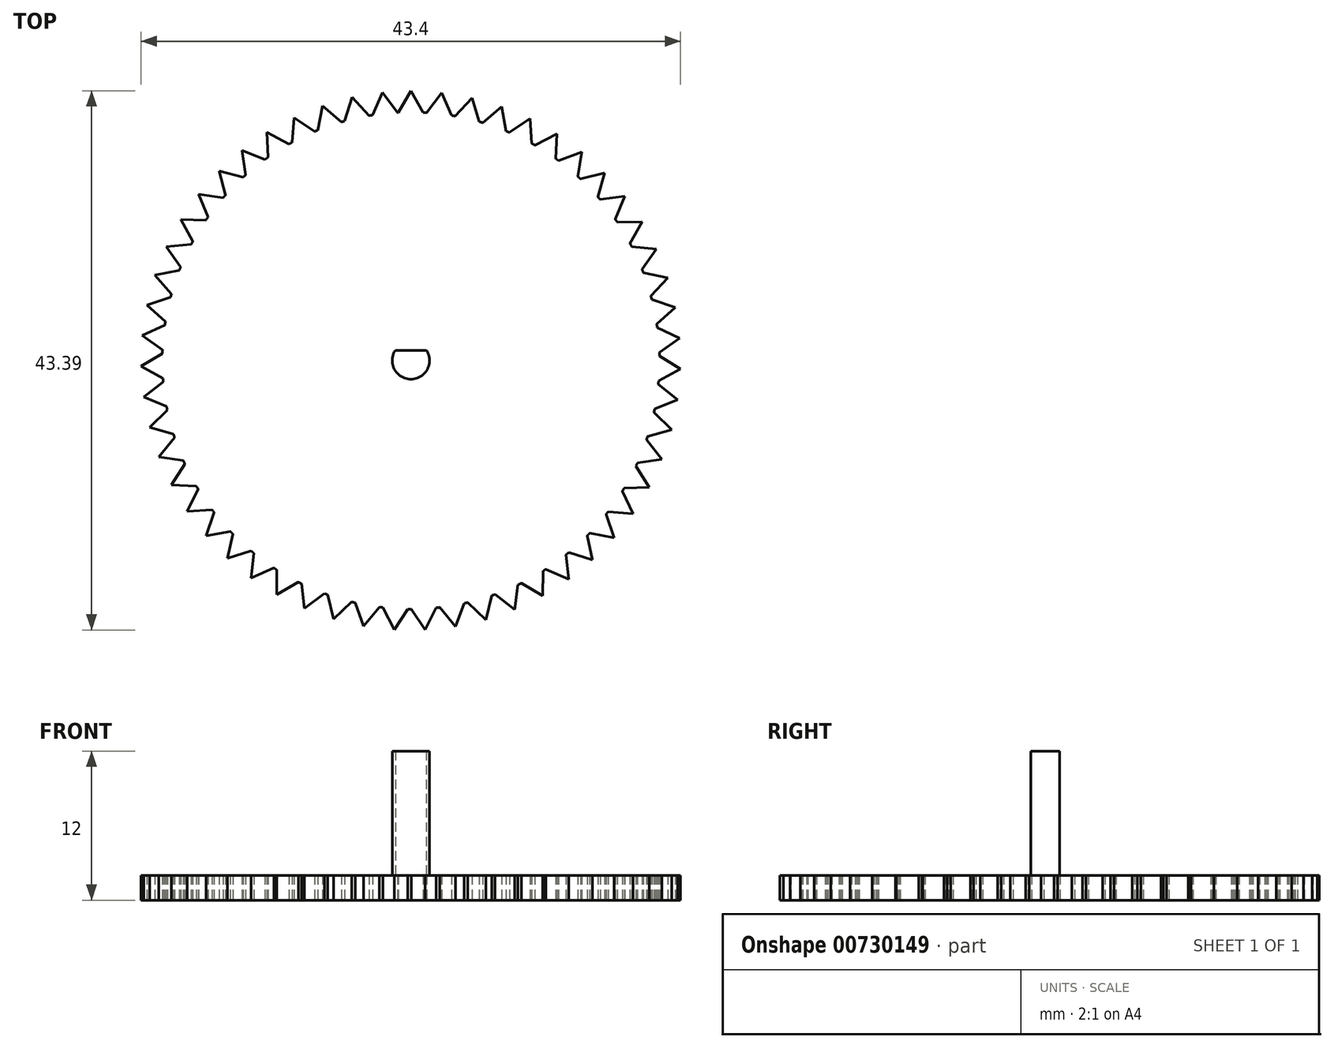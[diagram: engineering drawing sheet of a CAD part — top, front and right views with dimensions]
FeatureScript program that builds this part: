
annotation { "Feature Type Name" : "Feature", "Feature Type Description" : "" }
export const myFeature = defineFeature(function(context is Context, id is Id, definition is map)
    precondition{}
    {
        {
            var Q0;
            Q0=qCreatedBy(makeId("Top.planeOp"),FACE);
            var sketch = newSketch(context, id + "F0", { "sketchPlane" : qUnion([Q0])});
            skCircle(sketch, "E0", {"center": v(0, 0) * mm, "radius": 20 * mm});
            skLineSegment(sketch, "E1", {"start": v(-1, 19.97) * mm, "end": v(0, 21.7) * mm});
            skLineSegment(sketch, "E2", {"start": v(0, 21.7) * mm, "end": v(1, 19.97) * mm});
            skLineSegment(sketch, "E3.1.0", {"start": v(1.29, 19.96) * mm, "end": v(2.48, 21.57) * mm});
            skLineSegment(sketch, "E3.1.1", {"start": v(2.48, 21.57) * mm, "end": v(3.27, 19.73) * mm});
            skLineSegment(sketch, "E3.2.0", {"start": v(3.56, 19.68) * mm, "end": v(4.92, 21.14) * mm});
            skLineSegment(sketch, "E3.2.1", {"start": v(4.92, 21.14) * mm, "end": v(5.5, 19.23) * mm});
            skLineSegment(sketch, "E3.3.0", {"start": v(5.78, 19.15) * mm, "end": v(7.3, 20.44) * mm});
            skLineSegment(sketch, "E3.3.1", {"start": v(7.3, 20.44) * mm, "end": v(7.66, 18.47) * mm});
            skLineSegment(sketch, "E3.4.0", {"start": v(7.93, 18.36) * mm, "end": v(9.6, 19.47) * mm});
            skLineSegment(sketch, "E3.4.1", {"start": v(9.6, 19.47) * mm, "end": v(9.72, 17.48) * mm});
            skLineSegment(sketch, "E3.5.0", {"start": v(9.97, 17.34) * mm, "end": v(11.75, 18.25) * mm});
            skLineSegment(sketch, "E3.5.1", {"start": v(11.75, 18.25) * mm, "end": v(11.65, 16.25) * mm});
            skLineSegment(sketch, "E3.6.0", {"start": v(11.89, 16.08) * mm, "end": v(13.76, 16.79) * mm});
            skLineSegment(sketch, "E3.6.1", {"start": v(13.76, 16.79) * mm, "end": v(13.43, 14.82) * mm});
            skLineSegment(sketch, "E3.7.0", {"start": v(13.65, 14.62) * mm, "end": v(15.59, 15.1) * mm});
            skLineSegment(sketch, "E3.7.1", {"start": v(15.59, 15.1) * mm, "end": v(15.04, 13.19) * mm});
            skLineSegment(sketch, "E3.8.0", {"start": v(15.23, 12.97) * mm, "end": v(17.2, 13.23) * mm});
            skLineSegment(sketch, "E3.8.1", {"start": v(17.2, 13.23) * mm, "end": v(16.44, 11.38) * mm});
            skLineSegment(sketch, "E3.9.0", {"start": v(16.6, 11.15) * mm, "end": v(18.6, 11.18) * mm});
            skLineSegment(sketch, "E3.9.1", {"start": v(18.6, 11.18) * mm, "end": v(17.64, 9.43) * mm});
            skLineSegment(sketch, "E3.10.0", {"start": v(17.77, 9.18) * mm, "end": v(19.76, 8.98) * mm});
            skLineSegment(sketch, "E3.10.1", {"start": v(19.76, 8.98) * mm, "end": v(18.6, 7.36) * mm});
            skLineSegment(sketch, "E3.11.0", {"start": v(18.7, 7.09) * mm, "end": v(20.66, 6.67) * mm});
            skLineSegment(sketch, "E3.11.1", {"start": v(20.66, 6.67) * mm, "end": v(19.32, 5.18) * mm});
            skLineSegment(sketch, "E3.12.0", {"start": v(19.39, 4.9) * mm, "end": v(21.28, 4.27) * mm});
            skLineSegment(sketch, "E3.12.1", {"start": v(21.28, 4.27) * mm, "end": v(19.78, 2.94) * mm});
            skLineSegment(sketch, "E3.13.0", {"start": v(19.82, 2.66) * mm, "end": v(21.63, 1.8) * mm});
            skLineSegment(sketch, "E3.13.1", {"start": v(21.63, 1.8) * mm, "end": v(19.99, 0.67) * mm});
            skLineSegment(sketch, "E3.14.0", {"start": v(20, 0.38) * mm, "end": v(21.7, -0.67) * mm});
            skLineSegment(sketch, "E3.14.1", {"start": v(21.7, -0.67) * mm, "end": v(19.93, -1.62) * mm});
            skLineSegment(sketch, "E3.15.0", {"start": v(19.9, -1.9) * mm, "end": v(21.48, -3.15) * mm});
            skLineSegment(sketch, "E3.15.1", {"start": v(21.48, -3.15) * mm, "end": v(19.62, -3.88) * mm});
            skLineSegment(sketch, "E3.16.0", {"start": v(19.56, -4.17) * mm, "end": v(20.98, -5.58) * mm});
            skLineSegment(sketch, "E3.16.1", {"start": v(20.98, -5.58) * mm, "end": v(19.05, -6.1) * mm});
            skLineSegment(sketch, "E3.17.0", {"start": v(18.96, -6.37) * mm, "end": v(20.2, -7.94) * mm});
            skLineSegment(sketch, "E3.17.1", {"start": v(20.2, -7.94) * mm, "end": v(18.23, -8.23) * mm});
            skLineSegment(sketch, "E3.18.0", {"start": v(18.1, -8.5) * mm, "end": v(19.17, -10.2) * mm});
            skLineSegment(sketch, "E3.18.1", {"start": v(19.17, -10.2) * mm, "end": v(17.17, -10.26) * mm});
            skLineSegment(sketch, "E3.19.0", {"start": v(17.02, -10.5) * mm, "end": v(17.88, -12.31) * mm});
            skLineSegment(sketch, "E3.19.1", {"start": v(17.88, -12.31) * mm, "end": v(15.88, -12.15) * mm});
            skLineSegment(sketch, "E3.20.0", {"start": v(15.7, -12.38) * mm, "end": v(16.35, -14.27) * mm});
            skLineSegment(sketch, "E3.20.1", {"start": v(16.35, -14.27) * mm, "end": v(14.4, -13.89) * mm});
            skLineSegment(sketch, "E3.21.0", {"start": v(14.2, -14.1) * mm, "end": v(14.62, -16.05) * mm});
            skLineSegment(sketch, "E3.21.1", {"start": v(14.62, -16.05) * mm, "end": v(12.71, -15.44) * mm});
            skLineSegment(sketch, "E3.22.0", {"start": v(12.49, -15.62) * mm, "end": v(12.7, -17.61) * mm});
            skLineSegment(sketch, "E3.22.1", {"start": v(12.7, -17.61) * mm, "end": v(10.87, -16.8) * mm});
            skLineSegment(sketch, "E3.23.0", {"start": v(10.62, -16.94) * mm, "end": v(10.6, -18.94) * mm});
            skLineSegment(sketch, "E3.23.1", {"start": v(10.6, -18.94) * mm, "end": v(8.88, -17.92) * mm});
            skLineSegment(sketch, "E3.24.0", {"start": v(8.62, -18.05) * mm, "end": v(8.37, -20.03) * mm});
            skLineSegment(sketch, "E3.24.1", {"start": v(8.37, -20.03) * mm, "end": v(6.77, -18.82) * mm});
            skLineSegment(sketch, "E3.25.0", {"start": v(6.5, -18.91) * mm, "end": v(6.02, -20.85) * mm});
            skLineSegment(sketch, "E3.25.1", {"start": v(6.02, -20.85) * mm, "end": v(4.58, -19.47) * mm});
            skLineSegment(sketch, "E3.26.0", {"start": v(4.3, -19.53) * mm, "end": v(3.6, -21.4) * mm});
            skLineSegment(sketch, "E3.26.1", {"start": v(3.6, -21.4) * mm, "end": v(2.33, -19.86) * mm});
            skLineSegment(sketch, "E3.27.0", {"start": v(2.04, -19.9) * mm, "end": v(1.14, -21.68) * mm});
            skLineSegment(sketch, "E3.27.1", {"start": v(1.14, -21.68) * mm, "end": v(0.05, -20) * mm});
            skLineSegment(sketch, "E3.28.0", {"start": v(-0.24, -20) * mm, "end": v(-1.35, -21.67) * mm});
            skLineSegment(sketch, "E3.28.1", {"start": v(-1.35, -21.67) * mm, "end": v(-2.24, -19.87) * mm});
            skLineSegment(sketch, "E3.29.0", {"start": v(-2.52, -19.84) * mm, "end": v(-3.81, -21.37) * mm});
            skLineSegment(sketch, "E3.29.1", {"start": v(-3.81, -21.37) * mm, "end": v(-4.5, -19.49) * mm});
            skLineSegment(sketch, "E3.30.0", {"start": v(-4.77, -19.42) * mm, "end": v(-6.23, -20.8) * mm});
            skLineSegment(sketch, "E3.30.1", {"start": v(-6.23, -20.8) * mm, "end": v(-6.69, -18.85) * mm});
            skLineSegment(sketch, "E3.31.0", {"start": v(-6.96, -18.75) * mm, "end": v(-8.56, -19.95) * mm});
            skLineSegment(sketch, "E3.31.1", {"start": v(-8.56, -19.95) * mm, "end": v(-8.8, -17.96) * mm});
            skLineSegment(sketch, "E3.32.0", {"start": v(-9.05, -17.83) * mm, "end": v(-10.78, -18.84) * mm});
            skLineSegment(sketch, "E3.32.1", {"start": v(-10.78, -18.84) * mm, "end": v(-10.79, -16.84) * mm});
            skLineSegment(sketch, "E3.33.0", {"start": v(-11.03, -16.68) * mm, "end": v(-12.86, -17.49) * mm});
            skLineSegment(sketch, "E3.33.1", {"start": v(-12.86, -17.49) * mm, "end": v(-12.64, -15.5) * mm});
            skLineSegment(sketch, "E3.34.0", {"start": v(-12.86, -15.32) * mm, "end": v(-14.77, -15.9) * mm});
            skLineSegment(sketch, "E3.34.1", {"start": v(-14.77, -15.9) * mm, "end": v(-14.33, -13.95) * mm});
            skLineSegment(sketch, "E3.35.0", {"start": v(-14.53, -13.75) * mm, "end": v(-16.5, -14.11) * mm});
            skLineSegment(sketch, "E3.35.1", {"start": v(-16.5, -14.11) * mm, "end": v(-15.83, -12.23) * mm});
            skLineSegment(sketch, "E3.36.0", {"start": v(-16, -12) * mm, "end": v(-18, -12.14) * mm});
            skLineSegment(sketch, "E3.36.1", {"start": v(-18, -12.14) * mm, "end": v(-17.12, -10.34) * mm});
            skLineSegment(sketch, "E3.37.0", {"start": v(-17.27, -10.1) * mm, "end": v(-19.26, -10) * mm});
            skLineSegment(sketch, "E3.37.1", {"start": v(-19.26, -10) * mm, "end": v(-18.19, -8.32) * mm});
            skLineSegment(sketch, "E3.38.0", {"start": v(-18.3, -8.06) * mm, "end": v(-20.28, -7.74) * mm});
            skLineSegment(sketch, "E3.38.1", {"start": v(-20.28, -7.74) * mm, "end": v(-19.02, -6.19) * mm});
            skLineSegment(sketch, "E3.39.0", {"start": v(-19.1, -5.91) * mm, "end": v(-21.03, -5.37) * mm});
            skLineSegment(sketch, "E3.39.1", {"start": v(-21.03, -5.37) * mm, "end": v(-19.6, -3.98) * mm});
            skLineSegment(sketch, "E3.40.0", {"start": v(-19.66, -3.7) * mm, "end": v(-21.5, -2.94) * mm});
            skLineSegment(sketch, "E3.40.1", {"start": v(-21.5, -2.94) * mm, "end": v(-19.93, -1.71) * mm});
            skLineSegment(sketch, "E3.41.0", {"start": v(-19.95, -1.43) * mm, "end": v(-21.7, -0.46) * mm});
            skLineSegment(sketch, "E3.41.1", {"start": v(-21.7, -0.46) * mm, "end": v(-20, 0.57) * mm});
            skLineSegment(sketch, "E3.42.0", {"start": v(-19.98, 0.86) * mm, "end": v(-21.61, 2.02) * mm});
            skLineSegment(sketch, "E3.42.1", {"start": v(-21.61, 2.02) * mm, "end": v(-19.8, 2.85) * mm});
            skLineSegment(sketch, "E3.43.0", {"start": v(-19.75, 3.14) * mm, "end": v(-21.24, 4.47) * mm});
            skLineSegment(sketch, "E3.43.1", {"start": v(-21.24, 4.47) * mm, "end": v(-19.34, 5.1) * mm});
            skLineSegment(sketch, "E3.44.0", {"start": v(-19.27, 5.37) * mm, "end": v(-20.6, 6.87) * mm});
            skLineSegment(sketch, "E3.44.1", {"start": v(-20.6, 6.87) * mm, "end": v(-18.63, 7.27) * mm});
            skLineSegment(sketch, "E3.45.0", {"start": v(-18.53, 7.54) * mm, "end": v(-19.67, 9.17) * mm});
            skLineSegment(sketch, "E3.45.1", {"start": v(-19.67, 9.17) * mm, "end": v(-17.68, 9.35) * mm});
            skLineSegment(sketch, "E3.46.0", {"start": v(-17.54, 9.6) * mm, "end": v(-18.5, 11.36) * mm});
            skLineSegment(sketch, "E3.46.1", {"start": v(-18.5, 11.36) * mm, "end": v(-16.5, 11.3) * mm});
            skLineSegment(sketch, "E3.47.0", {"start": v(-16.33, 11.54) * mm, "end": v(-17.08, 13.4) * mm});
            skLineSegment(sketch, "E3.47.1", {"start": v(-17.08, 13.4) * mm, "end": v(-15.1, 13.12) * mm});
            skLineSegment(sketch, "E3.48.0", {"start": v(-14.9, 13.33) * mm, "end": v(-15.44, 15.26) * mm});
            skLineSegment(sketch, "E3.48.1", {"start": v(-15.44, 15.26) * mm, "end": v(-13.5, 14.75) * mm});
            skLineSegment(sketch, "E3.49.0", {"start": v(-13.29, 14.95) * mm, "end": v(-13.6, 16.92) * mm});
            skLineSegment(sketch, "E3.49.1", {"start": v(-13.6, 16.92) * mm, "end": v(-11.73, 16.2) * mm});
            skLineSegment(sketch, "E3.anchor1", {"start": v(0, 0) * mm, "end": v(-1, 19.97) * mm, "construction": true});
            skLineSegment(sketch, "E3.anchor2", {"start": v(0, 0) * mm, "end": v(-3.08, 19.76) * mm, "construction": true});
            skLineSegment(sketch, "E4.1.50.0", {"start": v(-11.5, 16.37) * mm, "end": v(-11.57, 18.36) * mm});
            skLineSegment(sketch, "E4.3.50.0", {"start": v(-11.57, 18.36) * mm, "end": v(-9.8, 17.43) * mm});
            skLineSegment(sketch, "E4.1.51.0", {"start": v(-9.55, 17.57) * mm, "end": v(-9.4, 19.57) * mm});
            skLineSegment(sketch, "E4.3.51.0", {"start": v(-9.4, 19.57) * mm, "end": v(-7.75, 18.44) * mm});
            skLineSegment(sketch, "E5.1.52.0", {"start": v(-7.48, 18.55) * mm, "end": v(-7.1, 20.51) * mm});
            skLineSegment(sketch, "E5.3.52.0", {"start": v(-7.1, 20.51) * mm, "end": v(-5.6, 19.2) * mm});
            skLineSegment(sketch, "E6.1.53.0", {"start": v(-5.32, 19.28) * mm, "end": v(-4.72, 21.19) * mm});
            skLineSegment(sketch, "E6.3.53.0", {"start": v(-4.72, 21.19) * mm, "end": v(-3.37, 19.71) * mm});
            skLineSegment(sketch, "E6.1.54.0", {"start": v(-3.08, 19.76) * mm, "end": v(-2.27, 21.59) * mm});
            skLineSegment(sketch, "E6.3.54.0", {"start": v(-2.27, 21.59) * mm, "end": v(-1.1, 19.97) * mm});
            skSolve(sketch);
        }
        {
            var Q0;
            {var subQ0=sQuery(id+"F0.wireOp",EDGE,"E0");var subQ136=makeQuery(id+"F0.imprint","INTERSECT",VERTEX,{"derivedFrom":[subQ0,sQuery(id+"F0.wireOp",EDGE,"E3.24.1")]});Q0=makeQuery(id+"F0.imprint","IMPRINT",FACE,{"disambiguationData":[TD([[makeQuery(id+"F0.imprint","IMPRINT",EDGE,{"disambiguationData":[TD([[subQ136,1.0]])],"derivedFrom":subQ0}),1.0]])]});}
            var Q1;
            {var subQ0=sQuery(id+"F0.wireOp",EDGE,"aa68531c-f383-4f58-aca5-e1ac582279db.1.62.0");Q1=makeQuery(id+"F0.imprint","IMPRINT",FACE,{"disambiguationData":[TD([[makeQuery(id+"F0.imprint","IMPRINT",EDGE,{"derivedFrom":subQ0}),-1.0]])]});}
            var Q2;
            {var subQ0=sQuery(id+"F0.wireOp",EDGE,"aa68531c-f383-4f58-aca5-e1ac582279db.1.74.0");Q2=makeQuery(id+"F0.imprint","IMPRINT",FACE,{"disambiguationData":[TD([[makeQuery(id+"F0.imprint","IMPRINT",EDGE,{"derivedFrom":subQ0}),-1.0]])]});}
            var Q3;
            {var subQ0=sQuery(id+"F0.wireOp",EDGE,"E3.28.0");Q3=makeQuery(id+"F0.imprint","IMPRINT",FACE,{"disambiguationData":[TD([[makeQuery(id+"F0.imprint","IMPRINT",EDGE,{"derivedFrom":subQ0}),-1.0]])]});}
            var Q4;
            {var subQ0=sQuery(id+"F0.wireOp",EDGE,"aa68531c-f383-4f58-aca5-e1ac582279db.1.58.0");Q4=makeQuery(id+"F0.imprint","IMPRINT",FACE,{"disambiguationData":[TD([[makeQuery(id+"F0.imprint","IMPRINT",EDGE,{"derivedFrom":subQ0}),-1.0]])]});}
            var Q5;
            {var subQ0=sQuery(id+"F0.wireOp",EDGE,"E3.8.0");Q5=makeQuery(id+"F0.imprint","IMPRINT",FACE,{"disambiguationData":[TD([[makeQuery(id+"F0.imprint","IMPRINT",EDGE,{"derivedFrom":subQ0}),-1.0]])]});}
            var Q6;
            {var subQ0=sQuery(id+"F0.wireOp",EDGE,"E3.7.0");Q6=makeQuery(id+"F0.imprint","IMPRINT",FACE,{"disambiguationData":[TD([[makeQuery(id+"F0.imprint","IMPRINT",EDGE,{"derivedFrom":subQ0}),-1.0]])]});}
            var Q7;
            {var subQ0=sQuery(id+"F0.wireOp",EDGE,"E3.26.0");Q7=makeQuery(id+"F0.imprint","IMPRINT",FACE,{"disambiguationData":[TD([[makeQuery(id+"F0.imprint","IMPRINT",EDGE,{"derivedFrom":subQ0}),-1.0]])]});}
            var Q8;
            {var subQ0=sQuery(id+"F0.wireOp",EDGE,"E3.42.0");Q8=makeQuery(id+"F0.imprint","IMPRINT",FACE,{"disambiguationData":[TD([[makeQuery(id+"F0.imprint","IMPRINT",EDGE,{"derivedFrom":subQ0}),-1.0]])]});}
            var Q9;
            {var subQ0=sQuery(id+"F0.wireOp",EDGE,"E3.6.0");Q9=makeQuery(id+"F0.imprint","IMPRINT",FACE,{"disambiguationData":[TD([[makeQuery(id+"F0.imprint","IMPRINT",EDGE,{"derivedFrom":subQ0}),-1.0]])]});}
            var Q10;
            {var subQ0=sQuery(id+"F0.wireOp",EDGE,"aa68531c-f383-4f58-aca5-e1ac582279db.1.73.0");Q10=makeQuery(id+"F0.imprint","IMPRINT",FACE,{"disambiguationData":[TD([[makeQuery(id+"F0.imprint","IMPRINT",EDGE,{"derivedFrom":subQ0}),-1.0]])]});}
            var Q11;
            {var subQ0=sQuery(id+"F0.wireOp",EDGE,"E3.41.0");Q11=makeQuery(id+"F0.imprint","IMPRINT",FACE,{"disambiguationData":[TD([[makeQuery(id+"F0.imprint","IMPRINT",EDGE,{"derivedFrom":subQ0}),-1.0]])]});}
            var Q12;
            {var subQ0=sQuery(id+"F0.wireOp",EDGE,"aa68531c-f383-4f58-aca5-e1ac582279db.1.59.0");Q12=makeQuery(id+"F0.imprint","IMPRINT",FACE,{"disambiguationData":[TD([[makeQuery(id+"F0.imprint","IMPRINT",EDGE,{"derivedFrom":subQ0}),-1.0]])]});}
            var Q13;
            {var subQ0=sQuery(id+"F0.wireOp",EDGE,"aa68531c-f383-4f58-aca5-e1ac582279db.1.91.0");Q13=makeQuery(id+"F0.imprint","IMPRINT",FACE,{"disambiguationData":[TD([[makeQuery(id+"F0.imprint","IMPRINT",EDGE,{"derivedFrom":subQ0}),-1.0]])]});}
            var Q14;
            {var subQ0=sQuery(id+"F0.wireOp",EDGE,"aa68531c-f383-4f58-aca5-e1ac582279db.1.75.0");Q14=makeQuery(id+"F0.imprint","IMPRINT",FACE,{"disambiguationData":[TD([[makeQuery(id+"F0.imprint","IMPRINT",EDGE,{"derivedFrom":subQ0}),-1.0]])]});}
            var Q15;
            {var subQ0=sQuery(id+"F0.wireOp",EDGE,"E3.10.0");Q15=makeQuery(id+"F0.imprint","IMPRINT",FACE,{"disambiguationData":[TD([[makeQuery(id+"F0.imprint","IMPRINT",EDGE,{"derivedFrom":subQ0}),-1.0]])]});}
            var Q16;
            {var subQ0=sQuery(id+"F0.wireOp",EDGE,"E3.20.0");Q16=makeQuery(id+"F0.imprint","IMPRINT",FACE,{"disambiguationData":[TD([[makeQuery(id+"F0.imprint","IMPRINT",EDGE,{"derivedFrom":subQ0}),-1.0]])]});}
            var Q17;
            {var subQ0=sQuery(id+"F0.wireOp",EDGE,"E3.11.0");Q17=makeQuery(id+"F0.imprint","IMPRINT",FACE,{"disambiguationData":[TD([[makeQuery(id+"F0.imprint","IMPRINT",EDGE,{"derivedFrom":subQ0}),-1.0]])]});}
            var Q18;
            {var subQ0=sQuery(id+"F0.wireOp",EDGE,"E3.27.0");Q18=makeQuery(id+"F0.imprint","IMPRINT",FACE,{"disambiguationData":[TD([[makeQuery(id+"F0.imprint","IMPRINT",EDGE,{"derivedFrom":subQ0}),-1.0]])]});}
            var Q19;
            {var subQ0=sQuery(id+"F0.wireOp",EDGE,"E3.22.0");Q19=makeQuery(id+"F0.imprint","IMPRINT",FACE,{"disambiguationData":[TD([[makeQuery(id+"F0.imprint","IMPRINT",EDGE,{"derivedFrom":subQ0}),-1.0]])]});}
            var Q20;
            {var subQ0=sQuery(id+"F0.wireOp",EDGE,"E3.21.0");Q20=makeQuery(id+"F0.imprint","IMPRINT",FACE,{"disambiguationData":[TD([[makeQuery(id+"F0.imprint","IMPRINT",EDGE,{"derivedFrom":subQ0}),-1.0]])]});}
            var Q21;
            {var subQ0=sQuery(id+"F0.wireOp",EDGE,"E3.40.0");Q21=makeQuery(id+"F0.imprint","IMPRINT",FACE,{"disambiguationData":[TD([[makeQuery(id+"F0.imprint","IMPRINT",EDGE,{"derivedFrom":subQ0}),-1.0]])]});}
            var Q22;
            {var subQ0=sQuery(id+"F0.wireOp",EDGE,"aa68531c-f383-4f58-aca5-e1ac582279db.1.92.0");Q22=makeQuery(id+"F0.imprint","IMPRINT",FACE,{"disambiguationData":[TD([[makeQuery(id+"F0.imprint","IMPRINT",EDGE,{"derivedFrom":subQ0}),-1.0]])]});}
            var Q23;
            {var subQ0=sQuery(id+"F0.wireOp",EDGE,"E3.4.0");Q23=makeQuery(id+"F0.imprint","IMPRINT",FACE,{"disambiguationData":[TD([[makeQuery(id+"F0.imprint","IMPRINT",EDGE,{"derivedFrom":subQ0}),-1.0]])]});}
            var Q24;
            {var subQ0=sQuery(id+"F0.wireOp",EDGE,"aa68531c-f383-4f58-aca5-e1ac582279db.1.68.0");Q24=makeQuery(id+"F0.imprint","IMPRINT",FACE,{"disambiguationData":[TD([[makeQuery(id+"F0.imprint","IMPRINT",EDGE,{"derivedFrom":subQ0}),-1.0]])]});}
            var Q25;
            {var subQ0=sQuery(id+"F0.wireOp",EDGE,"aa68531c-f383-4f58-aca5-e1ac582279db.1.67.0");Q25=makeQuery(id+"F0.imprint","IMPRINT",FACE,{"disambiguationData":[TD([[makeQuery(id+"F0.imprint","IMPRINT",EDGE,{"derivedFrom":subQ0}),-1.0]])]});}
            var Q26;
            {var subQ0=sQuery(id+"F0.wireOp",EDGE,"aa68531c-f383-4f58-aca5-e1ac582279db.1.57.0");Q26=makeQuery(id+"F0.imprint","IMPRINT",FACE,{"disambiguationData":[TD([[makeQuery(id+"F0.imprint","IMPRINT",EDGE,{"derivedFrom":subQ0}),-1.0]])]});}
            var Q27;
            {var subQ0=sQuery(id+"F0.wireOp",EDGE,"aa68531c-f383-4f58-aca5-e1ac582279db.1.89.0");Q27=makeQuery(id+"F0.imprint","IMPRINT",FACE,{"disambiguationData":[TD([[makeQuery(id+"F0.imprint","IMPRINT",EDGE,{"derivedFrom":subQ0}),-1.0]])]});}
            var Q28;
            {var subQ0=sQuery(id+"F0.wireOp",EDGE,"E3.24.0");Q28=makeQuery(id+"F0.imprint","IMPRINT",FACE,{"disambiguationData":[TD([[makeQuery(id+"F0.imprint","IMPRINT",EDGE,{"derivedFrom":subQ0}),-1.0]])]});}
            var Q29;
            {var subQ0=sQuery(id+"F0.wireOp",EDGE,"aa68531c-f383-4f58-aca5-e1ac582279db.1.83.0");Q29=makeQuery(id+"F0.imprint","IMPRINT",FACE,{"disambiguationData":[TD([[makeQuery(id+"F0.imprint","IMPRINT",EDGE,{"derivedFrom":subQ0}),-1.0]])]});}
            var Q30;
            {var subQ0=sQuery(id+"F0.wireOp",EDGE,"E3.5.0");Q30=makeQuery(id+"F0.imprint","IMPRINT",FACE,{"disambiguationData":[TD([[makeQuery(id+"F0.imprint","IMPRINT",EDGE,{"derivedFrom":subQ0}),-1.0]])]});}
            var Q31;
            {var subQ0=sQuery(id+"F0.wireOp",EDGE,"E3.2.0");Q31=makeQuery(id+"F0.imprint","IMPRINT",FACE,{"disambiguationData":[TD([[makeQuery(id+"F0.imprint","IMPRINT",EDGE,{"derivedFrom":subQ0}),-1.0]])]});}
            var Q32;
            {var subQ0=sQuery(id+"F0.wireOp",EDGE,"E3.9.0");Q32=makeQuery(id+"F0.imprint","IMPRINT",FACE,{"disambiguationData":[TD([[makeQuery(id+"F0.imprint","IMPRINT",EDGE,{"derivedFrom":subQ0}),-1.0]])]});}
            var Q33;
            {var subQ0=sQuery(id+"F0.wireOp",EDGE,"aa68531c-f383-4f58-aca5-e1ac582279db.1.70.0");Q33=makeQuery(id+"F0.imprint","IMPRINT",FACE,{"disambiguationData":[TD([[makeQuery(id+"F0.imprint","IMPRINT",EDGE,{"derivedFrom":subQ0}),-1.0]])]});}
            var Q34;
            {var subQ0=sQuery(id+"F0.wireOp",EDGE,"E3.25.0");Q34=makeQuery(id+"F0.imprint","IMPRINT",FACE,{"disambiguationData":[TD([[makeQuery(id+"F0.imprint","IMPRINT",EDGE,{"derivedFrom":subQ0}),-1.0]])]});}
            var Q35;
            {var subQ0=sQuery(id+"F0.wireOp",EDGE,"aa68531c-f383-4f58-aca5-e1ac582279db.1.72.0");Q35=makeQuery(id+"F0.imprint","IMPRINT",FACE,{"disambiguationData":[TD([[makeQuery(id+"F0.imprint","IMPRINT",EDGE,{"derivedFrom":subQ0}),-1.0]])]});}
            var Q36;
            {var subQ0=sQuery(id+"F0.wireOp",EDGE,"E3.19.0");Q36=makeQuery(id+"F0.imprint","IMPRINT",FACE,{"disambiguationData":[TD([[makeQuery(id+"F0.imprint","IMPRINT",EDGE,{"derivedFrom":subQ0}),-1.0]])]});}
            var Q37;
            {var subQ0=sQuery(id+"F0.wireOp",EDGE,"E3.18.0");Q37=makeQuery(id+"F0.imprint","IMPRINT",FACE,{"disambiguationData":[TD([[makeQuery(id+"F0.imprint","IMPRINT",EDGE,{"derivedFrom":subQ0}),-1.0]])]});}
            var Q38;
            {var subQ0=sQuery(id+"F0.wireOp",EDGE,"aa68531c-f383-4f58-aca5-e1ac582279db.1.77.0");Q38=makeQuery(id+"F0.imprint","IMPRINT",FACE,{"disambiguationData":[TD([[makeQuery(id+"F0.imprint","IMPRINT",EDGE,{"derivedFrom":subQ0}),-1.0]])]});}
            var Q39;
            {var subQ0=sQuery(id+"F0.wireOp",EDGE,"E3.36.0");Q39=makeQuery(id+"F0.imprint","IMPRINT",FACE,{"disambiguationData":[TD([[makeQuery(id+"F0.imprint","IMPRINT",EDGE,{"derivedFrom":subQ0}),-1.0]])]});}
            var Q40;
            {var subQ0=sQuery(id+"F0.wireOp",EDGE,"aa68531c-f383-4f58-aca5-e1ac582279db.1.76.0");Q40=makeQuery(id+"F0.imprint","IMPRINT",FACE,{"disambiguationData":[TD([[makeQuery(id+"F0.imprint","IMPRINT",EDGE,{"derivedFrom":subQ0}),-1.0]])]});}
            var Q41;
            {var subQ0=sQuery(id+"F0.wireOp",EDGE,"E1");Q41=makeQuery(id+"F0.imprint","IMPRINT",FACE,{"disambiguationData":[TD([[makeQuery(id+"F0.imprint","IMPRINT",EDGE,{"derivedFrom":subQ0}),-1.0]])]});}
            var Q42;
            {var subQ0=sQuery(id+"F0.wireOp",EDGE,"aa68531c-f383-4f58-aca5-e1ac582279db.1.90.0");Q42=makeQuery(id+"F0.imprint","IMPRINT",FACE,{"disambiguationData":[TD([[makeQuery(id+"F0.imprint","IMPRINT",EDGE,{"derivedFrom":subQ0}),-1.0]])]});}
            var Q43;
            {var subQ0=sQuery(id+"F0.wireOp",EDGE,"E3.32.0");Q43=makeQuery(id+"F0.imprint","IMPRINT",FACE,{"disambiguationData":[TD([[makeQuery(id+"F0.imprint","IMPRINT",EDGE,{"derivedFrom":subQ0}),-1.0]])]});}
            var Q44;
            {var subQ0=sQuery(id+"F0.wireOp",EDGE,"aa68531c-f383-4f58-aca5-e1ac582279db.1.96.0");Q44=makeQuery(id+"F0.imprint","IMPRINT",FACE,{"disambiguationData":[TD([[makeQuery(id+"F0.imprint","IMPRINT",EDGE,{"derivedFrom":subQ0}),-1.0]])]});}
            var Q45;
            {var subQ0=sQuery(id+"F0.wireOp",EDGE,"aa68531c-f383-4f58-aca5-e1ac582279db.1.80.0");Q45=makeQuery(id+"F0.imprint","IMPRINT",FACE,{"disambiguationData":[TD([[makeQuery(id+"F0.imprint","IMPRINT",EDGE,{"derivedFrom":subQ0}),-1.0]])]});}
            var Q46;
            {var subQ0=sQuery(id+"F0.wireOp",EDGE,"aa68531c-f383-4f58-aca5-e1ac582279db.1.64.0");Q46=makeQuery(id+"F0.imprint","IMPRINT",FACE,{"disambiguationData":[TD([[makeQuery(id+"F0.imprint","IMPRINT",EDGE,{"derivedFrom":subQ0}),-1.0]])]});}
            var Q47;
            {var subQ0=sQuery(id+"F0.wireOp",EDGE,"E3.33.0");Q47=makeQuery(id+"F0.imprint","IMPRINT",FACE,{"disambiguationData":[TD([[makeQuery(id+"F0.imprint","IMPRINT",EDGE,{"derivedFrom":subQ0}),-1.0]])]});}
            var Q48;
            {var subQ0=sQuery(id+"F0.wireOp",EDGE,"aa68531c-f383-4f58-aca5-e1ac582279db.1.97.0");Q48=makeQuery(id+"F0.imprint","IMPRINT",FACE,{"disambiguationData":[TD([[makeQuery(id+"F0.imprint","IMPRINT",EDGE,{"derivedFrom":subQ0}),-1.0]])]});}
            var Q49;
            {var subQ0=sQuery(id+"F0.wireOp",EDGE,"aa68531c-f383-4f58-aca5-e1ac582279db.1.81.0");Q49=makeQuery(id+"F0.imprint","IMPRINT",FACE,{"disambiguationData":[TD([[makeQuery(id+"F0.imprint","IMPRINT",EDGE,{"derivedFrom":subQ0}),-1.0]])]});}
            var Q50;
            {var subQ0=sQuery(id+"F0.wireOp",EDGE,"E3.15.0");Q50=makeQuery(id+"F0.imprint","IMPRINT",FACE,{"disambiguationData":[TD([[makeQuery(id+"F0.imprint","IMPRINT",EDGE,{"derivedFrom":subQ0}),-1.0]])]});}
            var Q51;
            {var subQ0=sQuery(id+"F0.wireOp",EDGE,"aa68531c-f383-4f58-aca5-e1ac582279db.1.69.0");Q51=makeQuery(id+"F0.imprint","IMPRINT",FACE,{"disambiguationData":[TD([[makeQuery(id+"F0.imprint","IMPRINT",EDGE,{"derivedFrom":subQ0}),-1.0]])]});}
            var Q52;
            {var subQ0=sQuery(id+"F0.wireOp",EDGE,"aa68531c-f383-4f58-aca5-e1ac582279db.1.85.0");Q52=makeQuery(id+"F0.imprint","IMPRINT",FACE,{"disambiguationData":[TD([[makeQuery(id+"F0.imprint","IMPRINT",EDGE,{"derivedFrom":subQ0}),-1.0]])]});}
            var Q53;
            {var subQ0=sQuery(id+"F0.wireOp",EDGE,"E3.1.0");Q53=makeQuery(id+"F0.imprint","IMPRINT",FACE,{"disambiguationData":[TD([[makeQuery(id+"F0.imprint","IMPRINT",EDGE,{"derivedFrom":subQ0}),-1.0]])]});}
            var Q54;
            {var subQ0=sQuery(id+"F0.wireOp",EDGE,"aa68531c-f383-4f58-aca5-e1ac582279db.1.88.0");Q54=makeQuery(id+"F0.imprint","IMPRINT",FACE,{"disambiguationData":[TD([[makeQuery(id+"F0.imprint","IMPRINT",EDGE,{"derivedFrom":subQ0}),-1.0]])]});}
            var Q55;
            {var subQ0=sQuery(id+"F0.wireOp",EDGE,"E3.23.0");Q55=makeQuery(id+"F0.imprint","IMPRINT",FACE,{"disambiguationData":[TD([[makeQuery(id+"F0.imprint","IMPRINT",EDGE,{"derivedFrom":subQ0}),-1.0]])]});}
            var Q56;
            {var subQ0=sQuery(id+"F0.wireOp",EDGE,"aa68531c-f383-4f58-aca5-e1ac582279db.1.60.0");Q56=makeQuery(id+"F0.imprint","IMPRINT",FACE,{"disambiguationData":[TD([[makeQuery(id+"F0.imprint","IMPRINT",EDGE,{"derivedFrom":subQ0}),-1.0]])]});}
            var Q57;
            {var subQ0=sQuery(id+"F0.wireOp",EDGE,"aa68531c-f383-4f58-aca5-e1ac582279db.1.93.0");Q57=makeQuery(id+"F0.imprint","IMPRINT",FACE,{"disambiguationData":[TD([[makeQuery(id+"F0.imprint","IMPRINT",EDGE,{"derivedFrom":subQ0}),-1.0]])]});}
            var Q58;
            {var subQ0=sQuery(id+"F0.wireOp",EDGE,"E3.29.0");Q58=makeQuery(id+"F0.imprint","IMPRINT",FACE,{"disambiguationData":[TD([[makeQuery(id+"F0.imprint","IMPRINT",EDGE,{"derivedFrom":subQ0}),-1.0]])]});}
            var Q59;
            {var subQ0=sQuery(id+"F0.wireOp",EDGE,"aa68531c-f383-4f58-aca5-e1ac582279db.1.86.0");Q59=makeQuery(id+"F0.imprint","IMPRINT",FACE,{"disambiguationData":[TD([[makeQuery(id+"F0.imprint","IMPRINT",EDGE,{"derivedFrom":subQ0}),-1.0]])]});}
            var Q60;
            {var subQ0=sQuery(id+"F0.wireOp",EDGE,"E3.35.0");Q60=makeQuery(id+"F0.imprint","IMPRINT",FACE,{"disambiguationData":[TD([[makeQuery(id+"F0.imprint","IMPRINT",EDGE,{"derivedFrom":subQ0}),-1.0]])]});}
            var Q61;
            {var subQ0=sQuery(id+"F0.wireOp",EDGE,"E3.37.0");Q61=makeQuery(id+"F0.imprint","IMPRINT",FACE,{"disambiguationData":[TD([[makeQuery(id+"F0.imprint","IMPRINT",EDGE,{"derivedFrom":subQ0}),-1.0]])]});}
            var Q62;
            {var subQ0=sQuery(id+"F0.wireOp",EDGE,"aa68531c-f383-4f58-aca5-e1ac582279db.1.66.0");Q62=makeQuery(id+"F0.imprint","IMPRINT",FACE,{"disambiguationData":[TD([[makeQuery(id+"F0.imprint","IMPRINT",EDGE,{"derivedFrom":subQ0}),-1.0]])]});}
            var Q63;
            {var subQ0=sQuery(id+"F0.wireOp",EDGE,"aa68531c-f383-4f58-aca5-e1ac582279db.1.82.0");Q63=makeQuery(id+"F0.imprint","IMPRINT",FACE,{"disambiguationData":[TD([[makeQuery(id+"F0.imprint","IMPRINT",EDGE,{"derivedFrom":subQ0}),-1.0]])]});}
            var Q64;
            {var subQ0=sQuery(id+"F0.wireOp",EDGE,"E3.13.0");Q64=makeQuery(id+"F0.imprint","IMPRINT",FACE,{"disambiguationData":[TD([[makeQuery(id+"F0.imprint","IMPRINT",EDGE,{"derivedFrom":subQ0}),-1.0]])]});}
            var Q65;
            {var subQ0=sQuery(id+"F0.wireOp",EDGE,"E3.14.0");Q65=makeQuery(id+"F0.imprint","IMPRINT",FACE,{"disambiguationData":[TD([[makeQuery(id+"F0.imprint","IMPRINT",EDGE,{"derivedFrom":subQ0}),-1.0]])]});}
            var Q66;
            {var subQ0=sQuery(id+"F0.wireOp",EDGE,"E3.16.0");Q66=makeQuery(id+"F0.imprint","IMPRINT",FACE,{"disambiguationData":[TD([[makeQuery(id+"F0.imprint","IMPRINT",EDGE,{"derivedFrom":subQ0}),-1.0]])]});}
            var Q67;
            {var subQ0=sQuery(id+"F0.wireOp",EDGE,"aa68531c-f383-4f58-aca5-e1ac582279db.1.98.0");Q67=makeQuery(id+"F0.imprint","IMPRINT",FACE,{"disambiguationData":[TD([[makeQuery(id+"F0.imprint","IMPRINT",EDGE,{"derivedFrom":subQ0}),-1.0]])]});}
            var Q68;
            {var subQ0=sQuery(id+"F0.wireOp",EDGE,"E3.34.0");Q68=makeQuery(id+"F0.imprint","IMPRINT",FACE,{"disambiguationData":[TD([[makeQuery(id+"F0.imprint","IMPRINT",EDGE,{"derivedFrom":subQ0}),-1.0]])]});}
            var Q69;
            {var subQ0=sQuery(id+"F0.wireOp",EDGE,"aa68531c-f383-4f58-aca5-e1ac582279db.1.63.0");Q69=makeQuery(id+"F0.imprint","IMPRINT",FACE,{"disambiguationData":[TD([[makeQuery(id+"F0.imprint","IMPRINT",EDGE,{"derivedFrom":subQ0}),-1.0]])]});}
            var Q70;
            {var subQ0=sQuery(id+"F0.wireOp",EDGE,"aa68531c-f383-4f58-aca5-e1ac582279db.1.79.0");Q70=makeQuery(id+"F0.imprint","IMPRINT",FACE,{"disambiguationData":[TD([[makeQuery(id+"F0.imprint","IMPRINT",EDGE,{"derivedFrom":subQ0}),-1.0]])]});}
            var Q71;
            {var subQ0=sQuery(id+"F0.wireOp",EDGE,"aa68531c-f383-4f58-aca5-e1ac582279db.1.95.0");Q71=makeQuery(id+"F0.imprint","IMPRINT",FACE,{"disambiguationData":[TD([[makeQuery(id+"F0.imprint","IMPRINT",EDGE,{"derivedFrom":subQ0}),-1.0]])]});}
            var Q72;
            {var subQ0=sQuery(id+"F0.wireOp",EDGE,"E3.31.0");Q72=makeQuery(id+"F0.imprint","IMPRINT",FACE,{"disambiguationData":[TD([[makeQuery(id+"F0.imprint","IMPRINT",EDGE,{"derivedFrom":subQ0}),-1.0]])]});}
            var Q73;
            {var subQ0=sQuery(id+"F0.wireOp",EDGE,"E3.17.0");Q73=makeQuery(id+"F0.imprint","IMPRINT",FACE,{"disambiguationData":[TD([[makeQuery(id+"F0.imprint","IMPRINT",EDGE,{"derivedFrom":subQ0}),-1.0]])]});}
            var Q74;
            {var subQ0=sQuery(id+"F0.wireOp",EDGE,"aa68531c-f383-4f58-aca5-e1ac582279db.1.65.0");Q74=makeQuery(id+"F0.imprint","IMPRINT",FACE,{"disambiguationData":[TD([[makeQuery(id+"F0.imprint","IMPRINT",EDGE,{"derivedFrom":subQ0}),-1.0]])]});}
            var Q75;
            {var subQ0=sQuery(id+"F0.wireOp",EDGE,"aa68531c-f383-4f58-aca5-e1ac582279db.1.78.0");Q75=makeQuery(id+"F0.imprint","IMPRINT",FACE,{"disambiguationData":[TD([[makeQuery(id+"F0.imprint","IMPRINT",EDGE,{"derivedFrom":subQ0}),-1.0]])]});}
            var Q76;
            {var subQ0=sQuery(id+"F0.wireOp",EDGE,"aa68531c-f383-4f58-aca5-e1ac582279db.1.94.0");Q76=makeQuery(id+"F0.imprint","IMPRINT",FACE,{"disambiguationData":[TD([[makeQuery(id+"F0.imprint","IMPRINT",EDGE,{"derivedFrom":subQ0}),-1.0]])]});}
            var Q77;
            {var subQ0=sQuery(id+"F0.wireOp",EDGE,"E3.30.0");Q77=makeQuery(id+"F0.imprint","IMPRINT",FACE,{"disambiguationData":[TD([[makeQuery(id+"F0.imprint","IMPRINT",EDGE,{"derivedFrom":subQ0}),-1.0]])]});}
            var Q78;
            {var subQ0=sQuery(id+"F0.wireOp",EDGE,"E3.3.0");Q78=makeQuery(id+"F0.imprint","IMPRINT",FACE,{"disambiguationData":[TD([[makeQuery(id+"F0.imprint","IMPRINT",EDGE,{"derivedFrom":subQ0}),-1.0]])]});}
            var Q79;
            {var subQ0=sQuery(id+"F0.wireOp",EDGE,"aa68531c-f383-4f58-aca5-e1ac582279db.1.71.0");Q79=makeQuery(id+"F0.imprint","IMPRINT",FACE,{"disambiguationData":[TD([[makeQuery(id+"F0.imprint","IMPRINT",EDGE,{"derivedFrom":subQ0}),-1.0]])]});}
            var Q80;
            {var subQ0=sQuery(id+"F0.wireOp",EDGE,"aa68531c-f383-4f58-aca5-e1ac582279db.1.87.0");Q80=makeQuery(id+"F0.imprint","IMPRINT",FACE,{"disambiguationData":[TD([[makeQuery(id+"F0.imprint","IMPRINT",EDGE,{"derivedFrom":subQ0}),-1.0]])]});}
            var Q81;
            {var subQ0=sQuery(id+"F0.wireOp",EDGE,"E3.43.0");Q81=makeQuery(id+"F0.imprint","IMPRINT",FACE,{"disambiguationData":[TD([[makeQuery(id+"F0.imprint","IMPRINT",EDGE,{"derivedFrom":subQ0}),-1.0]])]});}
            var Q82;
            {var subQ0=sQuery(id+"F0.wireOp",EDGE,"E3.12.0");Q82=makeQuery(id+"F0.imprint","IMPRINT",FACE,{"disambiguationData":[TD([[makeQuery(id+"F0.imprint","IMPRINT",EDGE,{"derivedFrom":subQ0}),-1.0]])]});}
            var Q83;
            {var subQ0=sQuery(id+"F0.wireOp",EDGE,"aa68531c-f383-4f58-aca5-e1ac582279db.1.84.0");Q83=makeQuery(id+"F0.imprint","IMPRINT",FACE,{"disambiguationData":[TD([[makeQuery(id+"F0.imprint","IMPRINT",EDGE,{"derivedFrom":subQ0}),-1.0]])]});}
            var Q84;
            {var subQ0=sQuery(id+"F0.wireOp",EDGE,"aa68531c-f383-4f58-aca5-e1ac582279db.1.99.0");Q84=makeQuery(id+"F0.imprint","IMPRINT",FACE,{"disambiguationData":[TD([[makeQuery(id+"F0.imprint","IMPRINT",EDGE,{"derivedFrom":subQ0}),-1.0]])]});}
            var Q85;
            {var subQ0=sQuery(id+"F0.wireOp",EDGE,"aa68531c-f383-4f58-aca5-e1ac582279db.1.51.0");Q85=makeQuery(id+"F0.imprint","IMPRINT",FACE,{"disambiguationData":[TD([[makeQuery(id+"F0.imprint","IMPRINT",EDGE,{"derivedFrom":subQ0}),-1.0]])]});}
            var Q86;
            {var subQ0=sQuery(id+"F0.wireOp",EDGE,"aa68531c-f383-4f58-aca5-e1ac582279db.1.56.0");Q86=makeQuery(id+"F0.imprint","IMPRINT",FACE,{"disambiguationData":[TD([[makeQuery(id+"F0.imprint","IMPRINT",EDGE,{"derivedFrom":subQ0}),-1.0]])]});}
            var Q87;
            {var subQ0=sQuery(id+"F0.wireOp",EDGE,"aa68531c-f383-4f58-aca5-e1ac582279db.1.52.0");Q87=makeQuery(id+"F0.imprint","IMPRINT",FACE,{"disambiguationData":[TD([[makeQuery(id+"F0.imprint","IMPRINT",EDGE,{"derivedFrom":subQ0}),-1.0]])]});}
            var Q88;
            {var subQ0=sQuery(id+"F0.wireOp",EDGE,"E3.38.0");Q88=makeQuery(id+"F0.imprint","IMPRINT",FACE,{"disambiguationData":[TD([[makeQuery(id+"F0.imprint","IMPRINT",EDGE,{"derivedFrom":subQ0}),-1.0]])]});}
            var Q89;
            {var subQ0=sQuery(id+"F0.wireOp",EDGE,"aa68531c-f383-4f58-aca5-e1ac582279db.1.54.0");Q89=makeQuery(id+"F0.imprint","IMPRINT",FACE,{"disambiguationData":[TD([[makeQuery(id+"F0.imprint","IMPRINT",EDGE,{"derivedFrom":subQ0}),-1.0]])]});}
            var Q90;
            {var subQ0=sQuery(id+"F0.wireOp",EDGE,"E3.49.0");Q90=makeQuery(id+"F0.imprint","IMPRINT",FACE,{"disambiguationData":[TD([[makeQuery(id+"F0.imprint","IMPRINT",EDGE,{"derivedFrom":subQ0}),-1.0]])]});}
            var Q91;
            {var subQ0=sQuery(id+"F0.wireOp",EDGE,"E3.45.0");Q91=makeQuery(id+"F0.imprint","IMPRINT",FACE,{"disambiguationData":[TD([[makeQuery(id+"F0.imprint","IMPRINT",EDGE,{"derivedFrom":subQ0}),-1.0]])]});}
            var Q92;
            {var subQ0=sQuery(id+"F0.wireOp",EDGE,"aa68531c-f383-4f58-aca5-e1ac582279db.1.53.0");Q92=makeQuery(id+"F0.imprint","IMPRINT",FACE,{"disambiguationData":[TD([[makeQuery(id+"F0.imprint","IMPRINT",EDGE,{"derivedFrom":subQ0}),-1.0]])]});}
            var Q93;
            {var subQ0=sQuery(id+"F0.wireOp",EDGE,"E3.47.0");Q93=makeQuery(id+"F0.imprint","IMPRINT",FACE,{"disambiguationData":[TD([[makeQuery(id+"F0.imprint","IMPRINT",EDGE,{"derivedFrom":subQ0}),-1.0]])]});}
            var Q94;
            {var subQ0=sQuery(id+"F0.wireOp",EDGE,"aa68531c-f383-4f58-aca5-e1ac582279db.1.55.0");Q94=makeQuery(id+"F0.imprint","IMPRINT",FACE,{"disambiguationData":[TD([[makeQuery(id+"F0.imprint","IMPRINT",EDGE,{"derivedFrom":subQ0}),-1.0]])]});}
            var Q95;
            {var subQ0=sQuery(id+"F0.wireOp",EDGE,"aa68531c-f383-4f58-aca5-e1ac582279db.1.50.0");Q95=makeQuery(id+"F0.imprint","IMPRINT",FACE,{"disambiguationData":[TD([[makeQuery(id+"F0.imprint","IMPRINT",EDGE,{"derivedFrom":subQ0}),-1.0]])]});}
            var Q96;
            {var subQ0=sQuery(id+"F0.wireOp",EDGE,"E3.48.0");Q96=makeQuery(id+"F0.imprint","IMPRINT",FACE,{"disambiguationData":[TD([[makeQuery(id+"F0.imprint","IMPRINT",EDGE,{"derivedFrom":subQ0}),-1.0]])]});}
            var Q97;
            {var subQ0=sQuery(id+"F0.wireOp",EDGE,"E3.39.0");Q97=makeQuery(id+"F0.imprint","IMPRINT",FACE,{"disambiguationData":[TD([[makeQuery(id+"F0.imprint","IMPRINT",EDGE,{"derivedFrom":subQ0}),-1.0]])]});}
            var Q98;
            {var subQ0=sQuery(id+"F0.wireOp",EDGE,"E3.44.0");Q98=makeQuery(id+"F0.imprint","IMPRINT",FACE,{"disambiguationData":[TD([[makeQuery(id+"F0.imprint","IMPRINT",EDGE,{"derivedFrom":subQ0}),-1.0]])]});}
            var Q99;
            {var subQ0=sQuery(id+"F0.wireOp",EDGE,"E3.46.0");Q99=makeQuery(id+"F0.imprint","IMPRINT",FACE,{"disambiguationData":[TD([[makeQuery(id+"F0.imprint","IMPRINT",EDGE,{"derivedFrom":subQ0}),-1.0]])]});}
            var Q100;
            {var subQ0=sQuery(id+"F0.wireOp",EDGE,"aa68531c-f383-4f58-aca5-e1ac582279db.1.61.0");Q100=makeQuery(id+"F0.imprint","IMPRINT",FACE,{"disambiguationData":[TD([[makeQuery(id+"F0.imprint","IMPRINT",EDGE,{"derivedFrom":subQ0}),-1.0]])]});}
            var Q101;
            {var subQ0=sQuery(id+"F0.wireOp",EDGE,"E4.1.50.0");Q101=makeQuery(id+"F0.imprint","IMPRINT",FACE,{"disambiguationData":[TD([[makeQuery(id+"F0.imprint","IMPRINT",EDGE,{"derivedFrom":subQ0}),-1.0]])]});}
            var Q102;
            {var subQ0=sQuery(id+"F0.wireOp",EDGE,"E4.1.51.0");Q102=makeQuery(id+"F0.imprint","IMPRINT",FACE,{"disambiguationData":[TD([[makeQuery(id+"F0.imprint","IMPRINT",EDGE,{"derivedFrom":subQ0}),-1.0]])]});}
            var Q103;
            {var subQ0=sQuery(id+"F0.wireOp",EDGE,"E5.1.52.0");Q103=makeQuery(id+"F0.imprint","IMPRINT",FACE,{"disambiguationData":[TD([[makeQuery(id+"F0.imprint","IMPRINT",EDGE,{"derivedFrom":subQ0}),-1.0]])]});}
            var Q104;
            {var subQ0=sQuery(id+"F0.wireOp",EDGE,"E6.1.53.0");Q104=makeQuery(id+"F0.imprint","IMPRINT",FACE,{"disambiguationData":[TD([[makeQuery(id+"F0.imprint","IMPRINT",EDGE,{"derivedFrom":subQ0}),-1.0]])]});}
            var Q105;
            {var subQ3=sQuery(id+"F0.wireOp",EDGE,"E6.1.54.0");Q105=makeQuery(id+"F0.imprint","IMPRINT",FACE,{"disambiguationData":[TD([[makeQuery(id+"F0.imprint","IMPRINT",EDGE,{"derivedFrom":subQ3}),-1.0]])]});}
            var Q106;
            {var subQ0=sQuery(id+"F0.wireOp",EDGE,"E2");Q106=makeQuery(id+"F0.imprint","IMPRINT",FACE,{"disambiguationData":[TD([[makeQuery(id+"F0.imprint","IMPRINT",EDGE,{"derivedFrom":subQ0}),-1.0]])]});}
            extrude(context, id + "F1", {"entities" : qUnion([Q0, Q1, Q2, Q3, Q4, Q5, Q6, Q7, Q8, Q9, Q10, Q11, Q12, Q13, Q14, Q15, Q16, Q17, Q18, Q19, Q20, Q21, Q22, Q23, Q24, Q25, Q26, Q27, Q28, Q29, Q30, Q31, Q32, Q33, Q34, Q35, Q36, Q37, Q38, Q39, Q40, Q41, Q42, Q43, Q44, Q45, Q46, Q47, Q48, Q49, Q50, Q51, Q52, Q53, Q54, Q55, Q56, Q57, Q58, Q59, Q60, Q61, Q62, Q63, Q64, Q65, Q66, Q67, Q68, Q69, Q70, Q71, Q72, Q73, Q74, Q75, Q76, Q77, Q78, Q79, Q80, Q81, Q82, Q83, Q84, Q85, Q86, Q87, Q88, Q89, Q90, Q91, Q92, Q93, Q94, Q95, Q96, Q97, Q98, Q99, Q100, Q101, Q102, Q103, Q104, Q105, Q106]), "depth" : 2 * mm, "offsetDistance" : 25 * mm});
        }
        {
            var Q0;
            Q0=makeQuery(id+"F1.opExtrude","CAP_FACE",FACE,{"disambiguationData":[OSD([sQuery(id+"F0.wireOp",EDGE,"E0"),sQuery(id+"F0.wireOp",EDGE,"E1"),sQuery(id+"F0.wireOp",EDGE,"E2"),sQuery(id+"F0.wireOp",EDGE,"E3.1.0"),sQuery(id+"F0.wireOp",EDGE,"E3.1.1"),sQuery(id+"F0.wireOp",EDGE,"E3.2.0"),sQuery(id+"F0.wireOp",EDGE,"E3.2.1"),sQuery(id+"F0.wireOp",EDGE,"E3.3.0"),sQuery(id+"F0.wireOp",EDGE,"E3.3.1"),sQuery(id+"F0.wireOp",EDGE,"E3.4.0"),sQuery(id+"F0.wireOp",EDGE,"E3.4.1"),sQuery(id+"F0.wireOp",EDGE,"E3.5.0"),sQuery(id+"F0.wireOp",EDGE,"E3.5.1"),sQuery(id+"F0.wireOp",EDGE,"E3.6.0"),sQuery(id+"F0.wireOp",EDGE,"E3.6.1"),sQuery(id+"F0.wireOp",EDGE,"E3.7.0"),sQuery(id+"F0.wireOp",EDGE,"E3.7.1"),sQuery(id+"F0.wireOp",EDGE,"E3.8.0"),sQuery(id+"F0.wireOp",EDGE,"E3.8.1"),sQuery(id+"F0.wireOp",EDGE,"E3.9.0"),sQuery(id+"F0.wireOp",EDGE,"E3.9.1"),sQuery(id+"F0.wireOp",EDGE,"E3.10.0"),sQuery(id+"F0.wireOp",EDGE,"E3.10.1"),sQuery(id+"F0.wireOp",EDGE,"E3.11.0"),sQuery(id+"F0.wireOp",EDGE,"E3.11.1"),sQuery(id+"F0.wireOp",EDGE,"E3.12.0"),sQuery(id+"F0.wireOp",EDGE,"E3.12.1"),sQuery(id+"F0.wireOp",EDGE,"E3.13.0"),sQuery(id+"F0.wireOp",EDGE,"E3.13.1"),sQuery(id+"F0.wireOp",EDGE,"E3.14.0"),sQuery(id+"F0.wireOp",EDGE,"E3.14.1"),sQuery(id+"F0.wireOp",EDGE,"E3.15.0"),sQuery(id+"F0.wireOp",EDGE,"E3.15.1"),sQuery(id+"F0.wireOp",EDGE,"E3.16.0"),sQuery(id+"F0.wireOp",EDGE,"E3.16.1"),sQuery(id+"F0.wireOp",EDGE,"E3.17.0"),sQuery(id+"F0.wireOp",EDGE,"E3.17.1"),sQuery(id+"F0.wireOp",EDGE,"E3.18.0"),sQuery(id+"F0.wireOp",EDGE,"E3.18.1"),sQuery(id+"F0.wireOp",EDGE,"E3.19.0"),sQuery(id+"F0.wireOp",EDGE,"E3.19.1"),sQuery(id+"F0.wireOp",EDGE,"E3.20.0"),sQuery(id+"F0.wireOp",EDGE,"E3.20.1"),sQuery(id+"F0.wireOp",EDGE,"E3.21.0"),sQuery(id+"F0.wireOp",EDGE,"E3.21.1"),sQuery(id+"F0.wireOp",EDGE,"E3.22.0"),sQuery(id+"F0.wireOp",EDGE,"E3.22.1"),sQuery(id+"F0.wireOp",EDGE,"E3.23.0"),sQuery(id+"F0.wireOp",EDGE,"E3.23.1"),sQuery(id+"F0.wireOp",EDGE,"E3.24.0"),sQuery(id+"F0.wireOp",EDGE,"E3.24.1"),sQuery(id+"F0.wireOp",EDGE,"E3.25.0"),sQuery(id+"F0.wireOp",EDGE,"E3.25.1"),sQuery(id+"F0.wireOp",EDGE,"E3.26.0"),sQuery(id+"F0.wireOp",EDGE,"E3.26.1"),sQuery(id+"F0.wireOp",EDGE,"E3.27.0"),sQuery(id+"F0.wireOp",EDGE,"E3.27.1"),sQuery(id+"F0.wireOp",EDGE,"E3.28.0"),sQuery(id+"F0.wireOp",EDGE,"E3.28.1"),sQuery(id+"F0.wireOp",EDGE,"E3.29.0"),sQuery(id+"F0.wireOp",EDGE,"E3.29.1"),sQuery(id+"F0.wireOp",EDGE,"E3.30.0"),sQuery(id+"F0.wireOp",EDGE,"E3.30.1"),sQuery(id+"F0.wireOp",EDGE,"E3.31.0"),sQuery(id+"F0.wireOp",EDGE,"E3.31.1"),sQuery(id+"F0.wireOp",EDGE,"E3.32.0"),sQuery(id+"F0.wireOp",EDGE,"E3.32.1"),sQuery(id+"F0.wireOp",EDGE,"E3.33.0"),sQuery(id+"F0.wireOp",EDGE,"E3.33.1"),sQuery(id+"F0.wireOp",EDGE,"E3.34.0"),sQuery(id+"F0.wireOp",EDGE,"E3.34.1"),sQuery(id+"F0.wireOp",EDGE,"E3.35.0"),sQuery(id+"F0.wireOp",EDGE,"E3.35.1"),sQuery(id+"F0.wireOp",EDGE,"E3.36.0"),sQuery(id+"F0.wireOp",EDGE,"E3.36.1"),sQuery(id+"F0.wireOp",EDGE,"E3.37.0"),sQuery(id+"F0.wireOp",EDGE,"E3.37.1"),sQuery(id+"F0.wireOp",EDGE,"E3.38.0"),sQuery(id+"F0.wireOp",EDGE,"E3.38.1"),sQuery(id+"F0.wireOp",EDGE,"E3.39.0"),sQuery(id+"F0.wireOp",EDGE,"E3.39.1"),sQuery(id+"F0.wireOp",EDGE,"E3.40.0"),sQuery(id+"F0.wireOp",EDGE,"E3.40.1"),sQuery(id+"F0.wireOp",EDGE,"E3.41.0"),sQuery(id+"F0.wireOp",EDGE,"E3.41.1"),sQuery(id+"F0.wireOp",EDGE,"E3.42.0"),sQuery(id+"F0.wireOp",EDGE,"E3.42.1"),sQuery(id+"F0.wireOp",EDGE,"E3.43.0"),sQuery(id+"F0.wireOp",EDGE,"E3.43.1"),sQuery(id+"F0.wireOp",EDGE,"E3.44.0"),sQuery(id+"F0.wireOp",EDGE,"E3.44.1"),sQuery(id+"F0.wireOp",EDGE,"E3.45.0"),sQuery(id+"F0.wireOp",EDGE,"E3.45.1"),sQuery(id+"F0.wireOp",EDGE,"E3.46.0"),sQuery(id+"F0.wireOp",EDGE,"E3.46.1"),sQuery(id+"F0.wireOp",EDGE,"E3.47.0"),sQuery(id+"F0.wireOp",EDGE,"E3.47.1"),sQuery(id+"F0.wireOp",EDGE,"E3.48.0"),sQuery(id+"F0.wireOp",EDGE,"E3.48.1"),sQuery(id+"F0.wireOp",EDGE,"E3.49.0"),sQuery(id+"F0.wireOp",EDGE,"E3.49.1"),sQuery(id+"F0.wireOp",EDGE,"aa68531c-f383-4f58-aca5-e1ac582279db.1.50.0"),sQuery(id+"F0.wireOp",EDGE,"aa68531c-f383-4f58-aca5-e1ac582279db.3.50.0"),sQuery(id+"F0.wireOp",EDGE,"aa68531c-f383-4f58-aca5-e1ac582279db.1.51.0"),sQuery(id+"F0.wireOp",EDGE,"aa68531c-f383-4f58-aca5-e1ac582279db.3.51.0"),sQuery(id+"F0.wireOp",EDGE,"aa68531c-f383-4f58-aca5-e1ac582279db.1.52.0"),sQuery(id+"F0.wireOp",EDGE,"aa68531c-f383-4f58-aca5-e1ac582279db.3.52.0"),sQuery(id+"F0.wireOp",EDGE,"aa68531c-f383-4f58-aca5-e1ac582279db.1.53.0"),sQuery(id+"F0.wireOp",EDGE,"aa68531c-f383-4f58-aca5-e1ac582279db.3.53.0"),sQuery(id+"F0.wireOp",EDGE,"aa68531c-f383-4f58-aca5-e1ac582279db.1.54.0"),sQuery(id+"F0.wireOp",EDGE,"aa68531c-f383-4f58-aca5-e1ac582279db.3.54.0"),sQuery(id+"F0.wireOp",EDGE,"aa68531c-f383-4f58-aca5-e1ac582279db.1.55.0"),sQuery(id+"F0.wireOp",EDGE,"aa68531c-f383-4f58-aca5-e1ac582279db.3.55.0"),sQuery(id+"F0.wireOp",EDGE,"aa68531c-f383-4f58-aca5-e1ac582279db.1.56.0"),sQuery(id+"F0.wireOp",EDGE,"aa68531c-f383-4f58-aca5-e1ac582279db.3.56.0"),sQuery(id+"F0.wireOp",EDGE,"aa68531c-f383-4f58-aca5-e1ac582279db.1.57.0"),sQuery(id+"F0.wireOp",EDGE,"aa68531c-f383-4f58-aca5-e1ac582279db.3.57.0"),sQuery(id+"F0.wireOp",EDGE,"aa68531c-f383-4f58-aca5-e1ac582279db.1.58.0"),sQuery(id+"F0.wireOp",EDGE,"aa68531c-f383-4f58-aca5-e1ac582279db.3.58.0"),sQuery(id+"F0.wireOp",EDGE,"aa68531c-f383-4f58-aca5-e1ac582279db.1.59.0"),sQuery(id+"F0.wireOp",EDGE,"aa68531c-f383-4f58-aca5-e1ac582279db.3.59.0"),sQuery(id+"F0.wireOp",EDGE,"aa68531c-f383-4f58-aca5-e1ac582279db.1.60.0"),sQuery(id+"F0.wireOp",EDGE,"aa68531c-f383-4f58-aca5-e1ac582279db.3.60.0"),sQuery(id+"F0.wireOp",EDGE,"aa68531c-f383-4f58-aca5-e1ac582279db.1.61.0"),sQuery(id+"F0.wireOp",EDGE,"aa68531c-f383-4f58-aca5-e1ac582279db.3.61.0"),sQuery(id+"F0.wireOp",EDGE,"aa68531c-f383-4f58-aca5-e1ac582279db.1.62.0"),sQuery(id+"F0.wireOp",EDGE,"aa68531c-f383-4f58-aca5-e1ac582279db.3.62.0"),sQuery(id+"F0.wireOp",EDGE,"aa68531c-f383-4f58-aca5-e1ac582279db.1.63.0"),sQuery(id+"F0.wireOp",EDGE,"aa68531c-f383-4f58-aca5-e1ac582279db.3.63.0"),sQuery(id+"F0.wireOp",EDGE,"aa68531c-f383-4f58-aca5-e1ac582279db.1.64.0"),sQuery(id+"F0.wireOp",EDGE,"aa68531c-f383-4f58-aca5-e1ac582279db.3.64.0"),sQuery(id+"F0.wireOp",EDGE,"aa68531c-f383-4f58-aca5-e1ac582279db.1.65.0"),sQuery(id+"F0.wireOp",EDGE,"aa68531c-f383-4f58-aca5-e1ac582279db.3.65.0"),sQuery(id+"F0.wireOp",EDGE,"aa68531c-f383-4f58-aca5-e1ac582279db.1.66.0"),sQuery(id+"F0.wireOp",EDGE,"aa68531c-f383-4f58-aca5-e1ac582279db.3.66.0"),sQuery(id+"F0.wireOp",EDGE,"aa68531c-f383-4f58-aca5-e1ac582279db.1.67.0"),sQuery(id+"F0.wireOp",EDGE,"aa68531c-f383-4f58-aca5-e1ac582279db.3.67.0"),sQuery(id+"F0.wireOp",EDGE,"aa68531c-f383-4f58-aca5-e1ac582279db.1.68.0"),sQuery(id+"F0.wireOp",EDGE,"aa68531c-f383-4f58-aca5-e1ac582279db.3.68.0"),sQuery(id+"F0.wireOp",EDGE,"aa68531c-f383-4f58-aca5-e1ac582279db.1.69.0"),sQuery(id+"F0.wireOp",EDGE,"aa68531c-f383-4f58-aca5-e1ac582279db.3.69.0"),sQuery(id+"F0.wireOp",EDGE,"aa68531c-f383-4f58-aca5-e1ac582279db.1.70.0"),sQuery(id+"F0.wireOp",EDGE,"aa68531c-f383-4f58-aca5-e1ac582279db.3.70.0"),sQuery(id+"F0.wireOp",EDGE,"aa68531c-f383-4f58-aca5-e1ac582279db.1.71.0"),sQuery(id+"F0.wireOp",EDGE,"aa68531c-f383-4f58-aca5-e1ac582279db.3.71.0"),sQuery(id+"F0.wireOp",EDGE,"aa68531c-f383-4f58-aca5-e1ac582279db.1.72.0"),sQuery(id+"F0.wireOp",EDGE,"aa68531c-f383-4f58-aca5-e1ac582279db.3.72.0"),sQuery(id+"F0.wireOp",EDGE,"aa68531c-f383-4f58-aca5-e1ac582279db.1.73.0"),sQuery(id+"F0.wireOp",EDGE,"aa68531c-f383-4f58-aca5-e1ac582279db.3.73.0"),sQuery(id+"F0.wireOp",EDGE,"aa68531c-f383-4f58-aca5-e1ac582279db.1.74.0"),sQuery(id+"F0.wireOp",EDGE,"aa68531c-f383-4f58-aca5-e1ac582279db.3.74.0"),sQuery(id+"F0.wireOp",EDGE,"aa68531c-f383-4f58-aca5-e1ac582279db.1.75.0"),sQuery(id+"F0.wireOp",EDGE,"aa68531c-f383-4f58-aca5-e1ac582279db.3.75.0"),sQuery(id+"F0.wireOp",EDGE,"aa68531c-f383-4f58-aca5-e1ac582279db.1.76.0"),sQuery(id+"F0.wireOp",EDGE,"aa68531c-f383-4f58-aca5-e1ac582279db.3.76.0"),sQuery(id+"F0.wireOp",EDGE,"aa68531c-f383-4f58-aca5-e1ac582279db.1.77.0"),sQuery(id+"F0.wireOp",EDGE,"aa68531c-f383-4f58-aca5-e1ac582279db.3.77.0"),sQuery(id+"F0.wireOp",EDGE,"aa68531c-f383-4f58-aca5-e1ac582279db.1.78.0"),sQuery(id+"F0.wireOp",EDGE,"aa68531c-f383-4f58-aca5-e1ac582279db.3.78.0"),sQuery(id+"F0.wireOp",EDGE,"aa68531c-f383-4f58-aca5-e1ac582279db.1.79.0"),sQuery(id+"F0.wireOp",EDGE,"aa68531c-f383-4f58-aca5-e1ac582279db.3.79.0"),sQuery(id+"F0.wireOp",EDGE,"aa68531c-f383-4f58-aca5-e1ac582279db.1.80.0"),sQuery(id+"F0.wireOp",EDGE,"aa68531c-f383-4f58-aca5-e1ac582279db.3.80.0"),sQuery(id+"F0.wireOp",EDGE,"aa68531c-f383-4f58-aca5-e1ac582279db.1.81.0"),sQuery(id+"F0.wireOp",EDGE,"aa68531c-f383-4f58-aca5-e1ac582279db.3.81.0"),sQuery(id+"F0.wireOp",EDGE,"aa68531c-f383-4f58-aca5-e1ac582279db.1.82.0"),sQuery(id+"F0.wireOp",EDGE,"aa68531c-f383-4f58-aca5-e1ac582279db.3.82.0"),sQuery(id+"F0.wireOp",EDGE,"aa68531c-f383-4f58-aca5-e1ac582279db.1.83.0"),sQuery(id+"F0.wireOp",EDGE,"aa68531c-f383-4f58-aca5-e1ac582279db.3.83.0"),sQuery(id+"F0.wireOp",EDGE,"aa68531c-f383-4f58-aca5-e1ac582279db.1.84.0"),sQuery(id+"F0.wireOp",EDGE,"aa68531c-f383-4f58-aca5-e1ac582279db.3.84.0"),sQuery(id+"F0.wireOp",EDGE,"aa68531c-f383-4f58-aca5-e1ac582279db.1.85.0"),sQuery(id+"F0.wireOp",EDGE,"aa68531c-f383-4f58-aca5-e1ac582279db.3.85.0"),sQuery(id+"F0.wireOp",EDGE,"aa68531c-f383-4f58-aca5-e1ac582279db.1.86.0"),sQuery(id+"F0.wireOp",EDGE,"aa68531c-f383-4f58-aca5-e1ac582279db.3.86.0"),sQuery(id+"F0.wireOp",EDGE,"aa68531c-f383-4f58-aca5-e1ac582279db.1.87.0"),sQuery(id+"F0.wireOp",EDGE,"aa68531c-f383-4f58-aca5-e1ac582279db.3.87.0"),sQuery(id+"F0.wireOp",EDGE,"aa68531c-f383-4f58-aca5-e1ac582279db.1.88.0"),sQuery(id+"F0.wireOp",EDGE,"aa68531c-f383-4f58-aca5-e1ac582279db.3.88.0"),sQuery(id+"F0.wireOp",EDGE,"aa68531c-f383-4f58-aca5-e1ac582279db.1.89.0"),sQuery(id+"F0.wireOp",EDGE,"aa68531c-f383-4f58-aca5-e1ac582279db.3.89.0"),sQuery(id+"F0.wireOp",EDGE,"aa68531c-f383-4f58-aca5-e1ac582279db.1.90.0"),sQuery(id+"F0.wireOp",EDGE,"aa68531c-f383-4f58-aca5-e1ac582279db.3.90.0"),sQuery(id+"F0.wireOp",EDGE,"aa68531c-f383-4f58-aca5-e1ac582279db.1.91.0"),sQuery(id+"F0.wireOp",EDGE,"aa68531c-f383-4f58-aca5-e1ac582279db.3.91.0"),sQuery(id+"F0.wireOp",EDGE,"aa68531c-f383-4f58-aca5-e1ac582279db.1.92.0"),sQuery(id+"F0.wireOp",EDGE,"aa68531c-f383-4f58-aca5-e1ac582279db.3.92.0"),sQuery(id+"F0.wireOp",EDGE,"aa68531c-f383-4f58-aca5-e1ac582279db.1.93.0"),sQuery(id+"F0.wireOp",EDGE,"aa68531c-f383-4f58-aca5-e1ac582279db.3.93.0"),sQuery(id+"F0.wireOp",EDGE,"aa68531c-f383-4f58-aca5-e1ac582279db.1.94.0"),sQuery(id+"F0.wireOp",EDGE,"aa68531c-f383-4f58-aca5-e1ac582279db.3.94.0"),sQuery(id+"F0.wireOp",EDGE,"aa68531c-f383-4f58-aca5-e1ac582279db.1.95.0"),sQuery(id+"F0.wireOp",EDGE,"aa68531c-f383-4f58-aca5-e1ac582279db.3.95.0"),sQuery(id+"F0.wireOp",EDGE,"aa68531c-f383-4f58-aca5-e1ac582279db.1.96.0"),sQuery(id+"F0.wireOp",EDGE,"aa68531c-f383-4f58-aca5-e1ac582279db.3.96.0"),sQuery(id+"F0.wireOp",EDGE,"aa68531c-f383-4f58-aca5-e1ac582279db.1.97.0"),sQuery(id+"F0.wireOp",EDGE,"aa68531c-f383-4f58-aca5-e1ac582279db.3.97.0"),sQuery(id+"F0.wireOp",EDGE,"aa68531c-f383-4f58-aca5-e1ac582279db.1.98.0"),sQuery(id+"F0.wireOp",EDGE,"aa68531c-f383-4f58-aca5-e1ac582279db.3.98.0"),sQuery(id+"F0.wireOp",EDGE,"aa68531c-f383-4f58-aca5-e1ac582279db.1.99.0"),sQuery(id+"F0.wireOp",EDGE,"aa68531c-f383-4f58-aca5-e1ac582279db.3.99.0")])],"isStart":false});
            var sketch = newSketch(context, id + "F2", { "sketchPlane" : qUnion([Q0])});
            skCircle(sketch, "E7", {"center": v(0, 0) * mm, "radius": 1.5 * mm});
            skLineSegment(sketch, "E8", {"start": v(-1.25, 0.83) * mm, "end": v(1.25, 0.83) * mm});
            skSolve(sketch);
        }
        {
            var Q0;
            {var subQ0=sQuery(id+"F2.wireOp",EDGE,"E8");Q0=makeQuery(id+"F2.imprint","IMPRINT",FACE,{"disambiguationData":[TD([[makeQuery(id+"F2.imprint","IMPRINT",EDGE,{"derivedFrom":subQ0}),-1.0]])]});}
            extrude(context, id + "F3", {"entities" : qUnion([Q0]), "operationType" : NewBodyOperationType.ADD, "depth" : 10 * mm, "offsetDistance" : 25 * mm});
        }
    });
